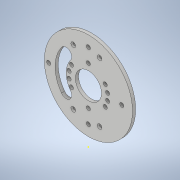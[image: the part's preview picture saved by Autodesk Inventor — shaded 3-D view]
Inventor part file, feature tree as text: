
AUTODESK INVENTOR PART (.ipt)
format: ipt  version: 2021 (Build 250183000, 183)  size: 335,872 bytes
history: native  units: in
note: dims shown in document units (in); Inventor stores cm internally (conversion verified against a paired STEP export)
features: sketch x11, move_body x10, extrude x8, direct_edit x4, hole x2, imported_body x1
ambient origin geometry x8: Origin, YZ Plane, XZ Plane, XY Plane, X Axis, Y Axis, Z Axis, Center Point
bodies: Solid1 (feature_tree)
feature tree (36):
  imported_body  "Imported1"
  extrude  "Extrusion1"  Depth=0.237in TaperAngle=0.0deg
  extrude  "Extrusion2"  Depth=11.5in
  direct_edit  "Direct Edit1"
  hole  "Hole1"  [1 undecoded]
  hole  "Hole5"  [1 undecoded]
  extrude  "Extrusion3"  TaperAngle=0.0deg  [1 undecoded]
  extrude  "Extrusion4"  Depth=0.24in TaperAngle=0.0deg
  direct_edit  "Direct Edit2"
  extrude  "Extrusion5"  TaperAngle=0.0deg  [1 undecoded]
  direct_edit  "Direct Edit3"
  extrude  "Extrusion6"  TaperAngle=0.0deg  [1 undecoded]
  direct_edit  "Direct Edit4"
  sketch  "Sketch21"  dims[d113=0.0in d114=0.0in d115=-0.013in d118=0.0in d119=0.0in d120=0.01in]
  extrude  "Extrusion9"  Depth=0.01in TaperAngle=0.0deg
  extrude  "Extrusion10"  Depth=0.01in TaperAngle=0.0deg
  sketch  "Sketch1"  dims[d0=1.0in d1=0.0in d2=0.237in d3=0.0in]
  sketch  "Sketch2"  dims[d4=0.0in d5=0.0in d6=0.0008in d7=11.5in]
  sketch  "Sketch4"  dims[d8=0.65in d9=0.75in d10=0.375in d11=0.25in d12=0.5635in d13=1.0in d14=0.8108in d15=4.205in]
  sketch  "Sketch8"  dims[d54=0.196in d55=0.5in d56=0.375in d57=0.25in d58=0.5635in d59=0.75in d60=0.0in d90=1.0in d91=0.0in]
  sketch  "Sketch14"  dims[d92=0.24in d93=0.0in d94=0.0in d95=0.0in d96=-0.003in]
  sketch  "Sketch15"  dims[d97=0.0in d98=0.0in d99=-0.003in d100=0.24in d101=0.0in]
  sketch  "Sketch16"  dims[d102=0.0in d103=0.0in d104=-0.003in d105=0.0in d106=0.0in d107=-0.003in]
  sketch  "Sketch17"  dims[d108=0.25in d109=0.0in d110=0.0in d111=0.0in d112=-0.013in]
  sketch  "Sketch22"  dims[d123=0.0in d124=0.0in d125=0.01in d126=0.0in d127=0.0in d128=0.01in]
  sketch  "Sketch23"  dims[d129=5.0in d130=0.1956in d131=0.1413in d132=0.1956in d133=0.1413in d139=1.0in d140=0.0in d141=5.25in d142=0.325in d143=1.5748in d145=0.0in d147=1.5748in d149=0.0in d151=1.5748in d153=0.0in d155=0.325in d156=0.325in d157=0.325in d158=0.5in d159=0.325in d160=1.0in d161=0.0in d28=1.0in d29=1.0in d30=1.0in d31=0.15in d32=0.25in d33=0.375in d34=32.2835in d35=0.75in d36=46.4567in d37=0.0625in d38=0.75in d39=0.375in]
  move_body  "Move1"
  move_body  "Move2"
  move_body  "Move3"
  move_body  "Move4"
  move_body  "Move5"
  move_body  "Move6"
  move_body  "Move7"
  move_body  "Move8"
  move_body  "Move9"
  move_body  "Move10"
note: 5 required parameter values undecoded (feature->parameter linkage not recoverable at this tier; creation-order binding heuristic only, values carry confidence <= 0.55)
